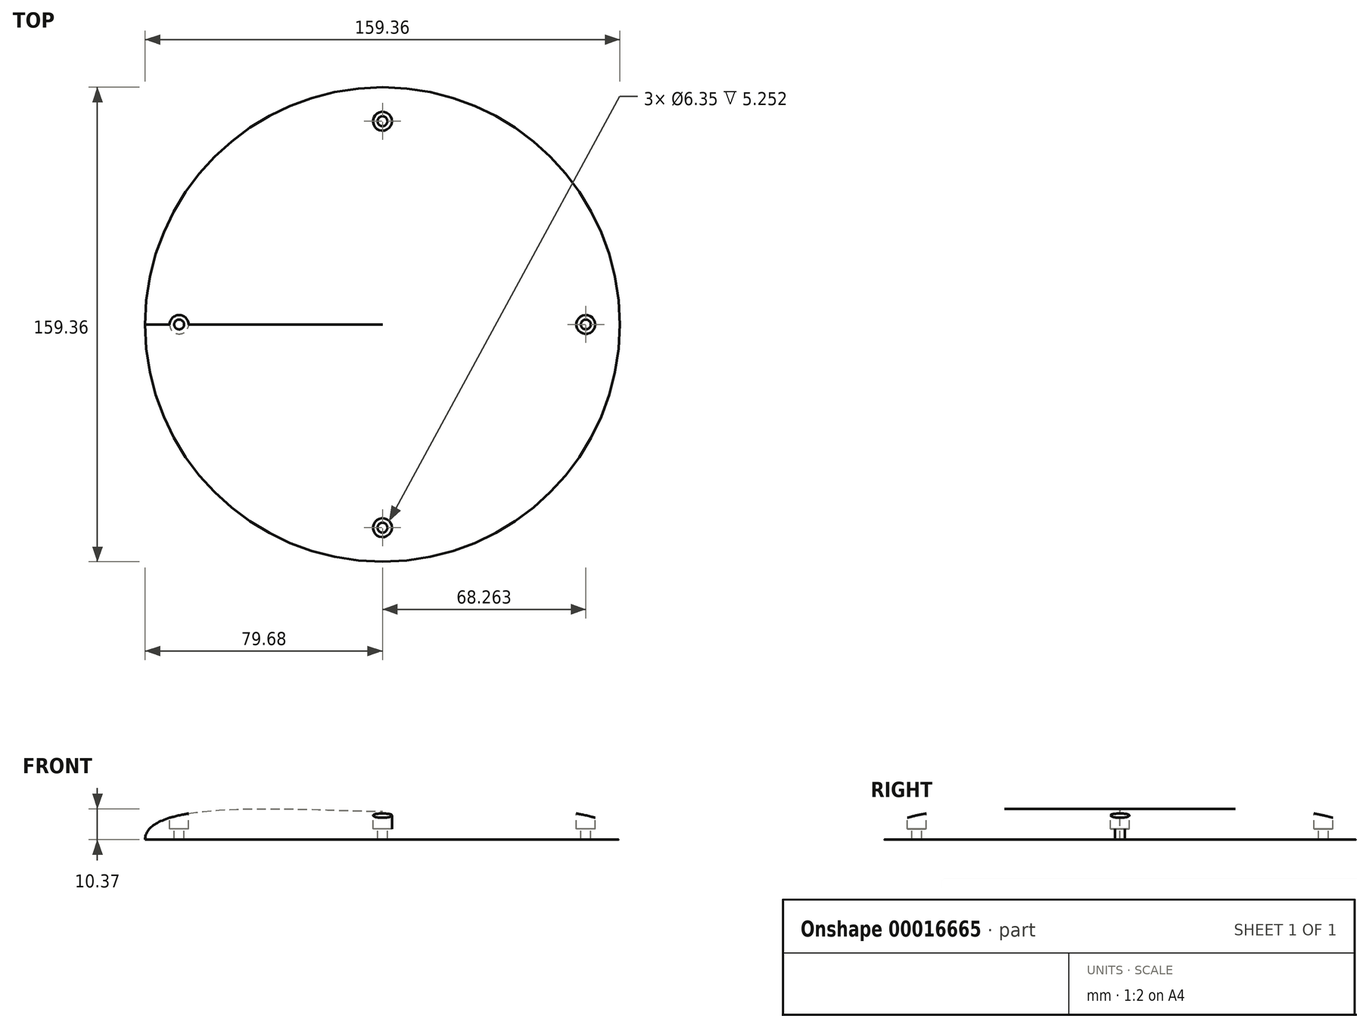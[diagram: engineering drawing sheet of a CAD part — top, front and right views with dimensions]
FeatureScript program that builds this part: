
annotation { "Feature Type Name" : "Feature", "Feature Type Description" : "" }
export const myFeature = defineFeature(function(context is Context, id is Id, definition is map)
    precondition{}
    {
        {
            var Q0;
            Q0=qCreatedBy(makeId("Front.planeOp"),FACE);
            var sketch = newSketch(context, id + "F0", { "sketchPlane" : qUnion([Q0])});
            skLineSegment(sketch, "E0", {"start": v(0, 0) * mm, "end": v(-79.68, 0) * mm});
            skLineSegment(sketch, "E1", {"start": v(0, 0) * mm, "end": v(0, 9.53) * mm});
            skFitSpline(sketch, "E2", {"points": [v(-79.68, 0) * mm, v(0, 9.53) * mm], "startDerivative": vector(0, 42.82) * mm, "endDerivative": vector(76.44, -0.62) * mm});
            skLineSegment(sketch, "E3", {"start": v(0, 0) * mm, "end": v(-10.8, -35.3) * mm, "construction": true});
            skSolve(sketch);
        }
        {
            var Q0;
            Q0=makeQuery(id+"F0.imprint","IMPRINT",FACE,{"disambiguationData":[TD([[makeQuery(id+"F0.imprint","IMPRINT",EDGE,{"derivedFrom":sQuery(id+"F0.wireOp",EDGE,"E0")}),-1.0]])]});
            var Q1;
            Q1=sQuery(id+"F0.wireOp",EDGE,"E1");
            revolve(context, id + "F1", {"entities" : qUnion([Q0]), "axis" : qUnion([Q1]), "revolveType" : RevolveType.FULL});
        }
        {
            var Q0;
            Q0=makeQuery(id+"F1.opRevolve","SWEPT_VERTEX",VERTEX,{"disambiguationData":[OSD([sQuery(id+"F0.wireOp",EDGE,"E1"),sQuery(id+"F0.wireOp",EDGE,"E2")])]});
            var Q1;
            Q1=qCreatedBy(makeId("Top.planeOp"),FACE);
            cPlane(context, id + "F2", {"entities" : qUnion([Q0, Q1]), "cplaneType" : CPlaneType.PLANE_POINT, "offset" : 152.4 * mm, "width" : 152.4 * mm, "height" : 152.4 * mm});
        }
        {
            var Q0;
            Q0=qCreatedBy(id+"F2.planeOp",FACE);
            var sketch = newSketch(context, id + "F3", { "sketchPlane" : qUnion([Q0])});
            skCircle(sketch, "E4", {"center": v(0, 0) * mm, "radius": 68.26 * mm, "construction": true});
            skPoint(sketch, "E5", {"position": v(0, 68.26) * mm});
            skPoint(sketch, "E6.1.0", {"position": v(68.26, 0) * mm});
            skPoint(sketch, "E6.2.0", {"position": v(0, -68.26) * mm});
            skPoint(sketch, "E6.3.0", {"position": v(-68.26, 0) * mm});
            skLineSegment(sketch, "E6.anchor1", {"start": v(0, 0) * mm, "end": v(0, 68.26) * mm, "construction": true});
            skLineSegment(sketch, "E6.anchor2", {"start": v(0, 0) * mm, "end": v(-68.26, 0) * mm, "construction": true});
            skSolve(sketch);
        }
        {
            var Q0;
            Q0=sQuery(id+"F3.wireOp",VERTEX,"E6.2.0");
            var Q1;
            Q1=sQuery(id+"F3.wireOp",VERTEX,"E6.1.0");
            var Q2;
            Q2=sQuery(id+"F3.wireOp",VERTEX,"E5");
            var Q3;
            Q3=sQuery(id+"F3.wireOp",VERTEX,"E6.3.0");
            var Q4;
            Q4=makeQuery(id+"F1.opRevolve","SWEPT_BODY",BODY,{"disambiguationData":[OSD([sQuery(id+"F0.wireOp",EDGE,"E0"),sQuery(id+"F0.wireOp",EDGE,"E1"),sQuery(id+"F0.wireOp",EDGE,"E2")])]});
            hole(context, id + "F4", {"style" : HoleStyle.C_BORE, "holeDiameter" : 3.3 * mm, "cBoreDiameter" : 6.35 * mm, "cBoreDepth" : 3.8 * mm, "endStyle" : HoleEndStyle.THROUGH, "locations" : qUnion([Q0, Q1, Q2, Q3]), "scope" : qUnion([Q4])});
        }
    });
